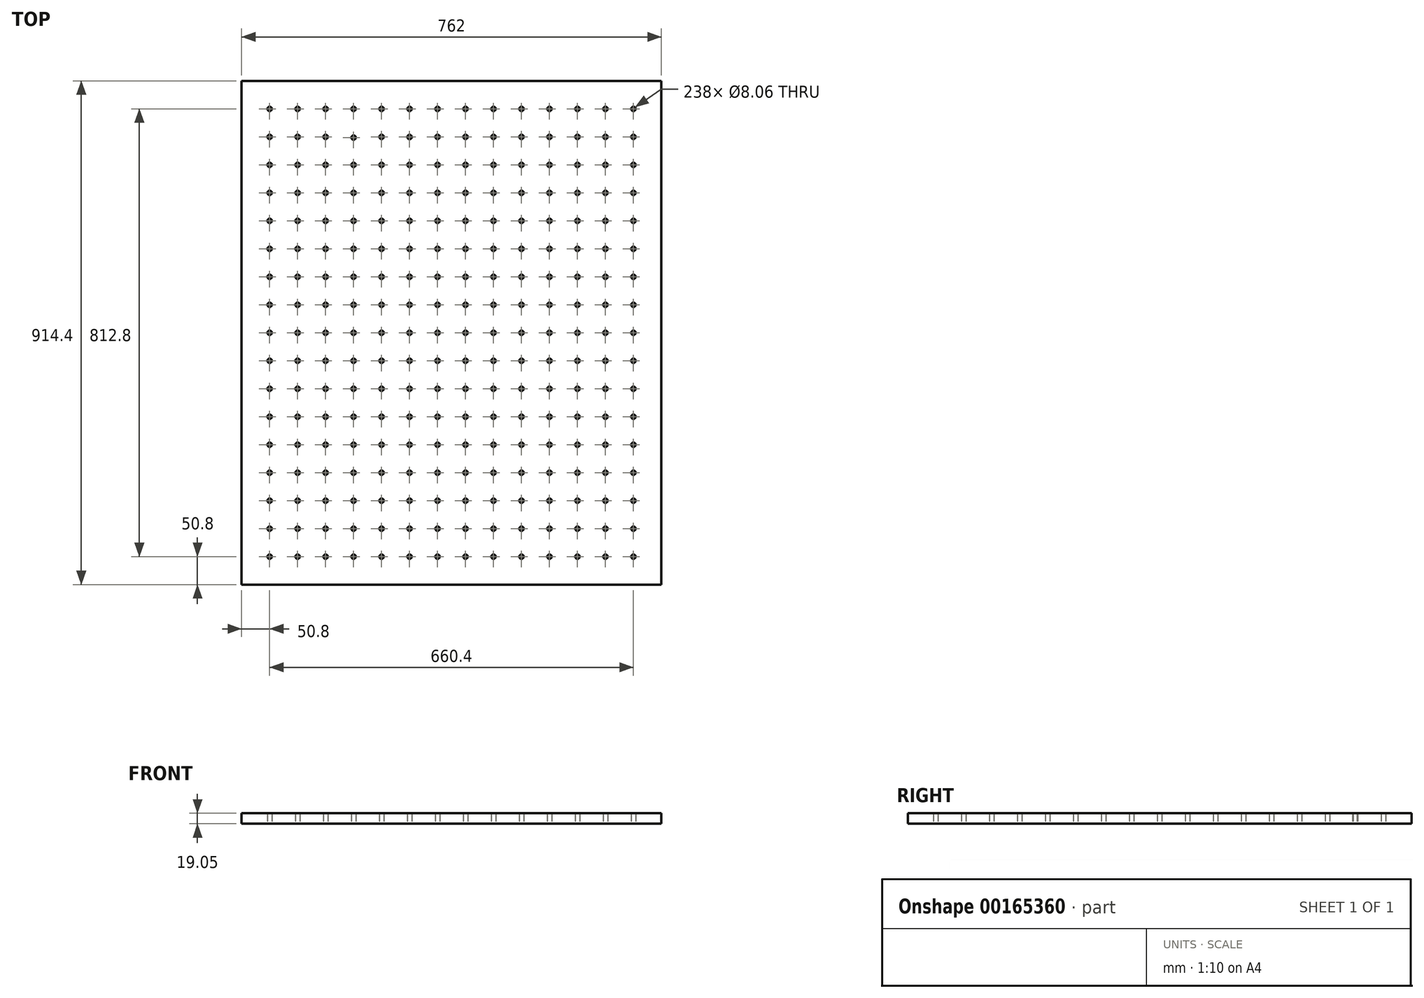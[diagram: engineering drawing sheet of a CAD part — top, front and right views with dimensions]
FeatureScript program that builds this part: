
annotation { "Feature Type Name" : "Feature", "Feature Type Description" : "" }
export const myFeature = defineFeature(function(context is Context, id is Id, definition is map)
    precondition{}
    {
        {
            var Q0;
            Q0=qCreatedBy(makeId("Top.planeOp"),FACE);
            var sketch = newSketch(context, id + "F0", { "sketchPlane" : qUnion([Q0])});
            skLineSegment(sketch, "E0.rect.bottom", {"start": v(381, -457.2) * mm, "end": v(-381, -457.2) * mm});
            skLineSegment(sketch, "E0.rect.top", {"start": v(381, 457.2) * mm, "end": v(-381, 457.2) * mm});
            skLineSegment(sketch, "E0.rect.left", {"start": v(381, -457.2) * mm, "end": v(381, 457.2) * mm});
            skLineSegment(sketch, "E0.rect.right", {"start": v(-381, -457.2) * mm, "end": v(-381, 457.2) * mm});
            skPoint(sketch, "E0.rect.middle", {"position": v(0, 0) * mm});
            skLineSegment(sketch, "E1", {"start": v(-381, 406.4) * mm, "end": v(381, 406.4) * mm, "construction": true});
            skLineSegment(sketch, "E2", {"start": v(381, 406.4) * mm, "end": v(378.47, 409.6) * mm, "construction": true});
            skLineSegment(sketch, "E3", {"start": v(-381, 355.6) * mm, "end": v(381, 355.6) * mm, "construction": true});
            skLineSegment(sketch, "E4", {"start": v(-381, 304.8) * mm, "end": v(381, 304.8) * mm, "construction": true});
            skLineSegment(sketch, "E5", {"start": v(-381, 254) * mm, "end": v(381, 254) * mm, "construction": true});
            skLineSegment(sketch, "E6", {"start": v(-381, 203.2) * mm, "end": v(381, 203.2) * mm, "construction": true});
            skLineSegment(sketch, "E7", {"start": v(-381, 152.4) * mm, "end": v(381, 152.4) * mm, "construction": true});
            skLineSegment(sketch, "E8", {"start": v(-381, 0) * mm, "end": v(381, 0) * mm, "construction": true});
            skLineSegment(sketch, "E9", {"start": v(-381, -50.8) * mm, "end": v(381, -50.8) * mm, "construction": true});
            skLineSegment(sketch, "E10", {"start": v(-381, -101.6) * mm, "end": v(381, -101.6) * mm, "construction": true});
            skLineSegment(sketch, "E11", {"start": v(-381, -152.4) * mm, "end": v(381, -152.4) * mm, "construction": true});
            skLineSegment(sketch, "E12", {"start": v(-330.2, -457.2) * mm, "end": v(-330.2, 457.2) * mm, "construction": true});
            skLineSegment(sketch, "E13", {"start": v(-279.4, 457.2) * mm, "end": v(-279.4, -457.2) * mm, "construction": true});
            skLineSegment(sketch, "E14", {"start": v(-228.6, 457.2) * mm, "end": v(-228.6, -457.2) * mm, "construction": true});
            skLineSegment(sketch, "E15", {"start": v(-177.8, -457.2) * mm, "end": v(-177.8, 457.2) * mm, "construction": true});
            skLineSegment(sketch, "E16", {"start": v(-127, 457.2) * mm, "end": v(-127, -457.2) * mm, "construction": true});
            skLineSegment(sketch, "E17", {"start": v(-76.2, 457.2) * mm, "end": v(-76.2, -457.2) * mm, "construction": true});
            skLineSegment(sketch, "E18", {"start": v(-25.4, 457.2) * mm, "end": v(-25.4, -457.2) * mm, "construction": true});
            skLineSegment(sketch, "E19", {"start": v(25.4, 457.2) * mm, "end": v(25.4, -457.2) * mm, "construction": true});
            skLineSegment(sketch, "E20", {"start": v(76.2, 457.2) * mm, "end": v(76.2, -457.2) * mm, "construction": true});
            skLineSegment(sketch, "E21", {"start": v(127, 457.2) * mm, "end": v(127, -457.2) * mm, "construction": true});
            skLineSegment(sketch, "E22", {"start": v(177.8, 457.2) * mm, "end": v(177.8, -457.2) * mm, "construction": true});
            skLineSegment(sketch, "E23", {"start": v(228.6, 457.2) * mm, "end": v(228.6, -457.2) * mm, "construction": true});
            skLineSegment(sketch, "E24", {"start": v(-381, -203.2) * mm, "end": v(381, -203.2) * mm, "construction": true});
            skLineSegment(sketch, "E25", {"start": v(-381, -254) * mm, "end": v(381, -254) * mm, "construction": true});
            skLineSegment(sketch, "E26", {"start": v(-381, -304.8) * mm, "end": v(381, -304.8) * mm, "construction": true});
            skLineSegment(sketch, "E27", {"start": v(-381, -355.6) * mm, "end": v(381, -355.6) * mm, "construction": true});
            skLineSegment(sketch, "E28", {"start": v(-381, -406.4) * mm, "end": v(381, -406.4) * mm, "construction": true});
            skLineSegment(sketch, "E29", {"start": v(-381, 101.6) * mm, "end": v(381, 101.6) * mm, "construction": true});
            skLineSegment(sketch, "E30", {"start": v(-381, 50.8) * mm, "end": v(381, 50.8) * mm, "construction": true});
            skLineSegment(sketch, "E31", {"start": v(279.4, 457.2) * mm, "end": v(279.4, -457.2) * mm, "construction": true});
            skLineSegment(sketch, "E32", {"start": v(330.2, 457.2) * mm, "end": v(330.2, -457.2) * mm, "construction": true});
            skCircle(sketch, "E33", {"center": v(-330.2, 406.4) * mm, "radius": 4.03 * mm});
            skCircle(sketch, "E34", {"center": v(-279.4, 406.4) * mm, "radius": 4.03 * mm});
            skCircle(sketch, "E35", {"center": v(-228.6, 406.4) * mm, "radius": 4.03 * mm});
            skCircle(sketch, "E36", {"center": v(-177.8, 406.4) * mm, "radius": 4.03 * mm});
            skCircle(sketch, "E37", {"center": v(-127, 406.4) * mm, "radius": 4.03 * mm});
            skCircle(sketch, "E38", {"center": v(-76.2, 406.4) * mm, "radius": 4.03 * mm});
            skCircle(sketch, "E39", {"center": v(-25.4, 406.4) * mm, "radius": 4.03 * mm});
            skCircle(sketch, "E40", {"center": v(25.4, 406.4) * mm, "radius": 4.03 * mm});
            skCircle(sketch, "E41", {"center": v(76.2, 406.4) * mm, "radius": 4.03 * mm});
            skCircle(sketch, "E42", {"center": v(127, 406.4) * mm, "radius": 4.03 * mm});
            skCircle(sketch, "E43", {"center": v(177.8, 406.4) * mm, "radius": 4.03 * mm});
            skCircle(sketch, "E44", {"center": v(-330.2, 355.6) * mm, "radius": 4.03 * mm});
            skCircle(sketch, "E45", {"center": v(-279.4, 355.6) * mm, "radius": 4.03 * mm});
            skCircle(sketch, "E46", {"center": v(-228.6, 355.6) * mm, "radius": 4.03 * mm});
            skCircle(sketch, "E47", {"center": v(-177.8, 354.31) * mm, "radius": 4.03 * mm});
            skCircle(sketch, "E48", {"center": v(-127, 355.6) * mm, "radius": 4.03 * mm});
            skCircle(sketch, "E49", {"center": v(-76.2, 355.32) * mm, "radius": 4.03 * mm});
            skCircle(sketch, "E50", {"center": v(-25.4, 355.6) * mm, "radius": 4.03 * mm});
            skCircle(sketch, "E51", {"center": v(25.4, 355.6) * mm, "radius": 4.03 * mm});
            skCircle(sketch, "E52", {"center": v(76.2, 355.6) * mm, "radius": 4.03 * mm});
            skCircle(sketch, "E53", {"center": v(127, 355.6) * mm, "radius": 4.03 * mm});
            skCircle(sketch, "E54", {"center": v(177.8, 355.6) * mm, "radius": 4.03 * mm});
            skCircle(sketch, "E55", {"center": v(228.6, 355.6) * mm, "radius": 4.03 * mm});
            skCircle(sketch, "E56", {"center": v(228.6, 304.8) * mm, "radius": 4.03 * mm});
            skCircle(sketch, "E57", {"center": v(177.8, 304.8) * mm, "radius": 4.03 * mm});
            skCircle(sketch, "E58", {"center": v(127, 304.8) * mm, "radius": 4.03 * mm});
            skCircle(sketch, "E59", {"center": v(76.2, 304.8) * mm, "radius": 4.03 * mm});
            skCircle(sketch, "E60", {"center": v(-330.2, 304.8) * mm, "radius": 4.03 * mm});
            skCircle(sketch, "E61", {"center": v(-279.4, 304.8) * mm, "radius": 4.03 * mm});
            skCircle(sketch, "E62", {"center": v(-228.6, 304.8) * mm, "radius": 4.03 * mm});
            skCircle(sketch, "E63", {"center": v(-177.8, 304.8) * mm, "radius": 4.03 * mm});
            skCircle(sketch, "E64", {"center": v(-127, 304.8) * mm, "radius": 4.03 * mm});
            skCircle(sketch, "E65", {"center": v(-76.2, 304.8) * mm, "radius": 4.03 * mm});
            skCircle(sketch, "E66", {"center": v(-25.4, 304.8) * mm, "radius": 4.03 * mm});
            skCircle(sketch, "E67", {"center": v(25.4, 304.8) * mm, "radius": 4.03 * mm});
            skCircle(sketch, "E68", {"center": v(-330.2, 254) * mm, "radius": 4.03 * mm});
            skCircle(sketch, "E69", {"center": v(-279.4, 254) * mm, "radius": 4.03 * mm});
            skCircle(sketch, "E70", {"center": v(-228.6, 254) * mm, "radius": 4.03 * mm});
            skCircle(sketch, "E71", {"center": v(-177.8, 254) * mm, "radius": 4.03 * mm});
            skCircle(sketch, "E72", {"center": v(-127, 254) * mm, "radius": 4.03 * mm});
            skCircle(sketch, "E73", {"center": v(-76.2, 254) * mm, "radius": 4.03 * mm});
            skCircle(sketch, "E74", {"center": v(-25.4, 254) * mm, "radius": 4.03 * mm});
            skCircle(sketch, "E75", {"center": v(25.4, 254) * mm, "radius": 4.03 * mm});
            skCircle(sketch, "E76", {"center": v(76.2, 254) * mm, "radius": 4.03 * mm});
            skCircle(sketch, "E77", {"center": v(127, 254) * mm, "radius": 4.03 * mm});
            skCircle(sketch, "E78", {"center": v(177.8, 254) * mm, "radius": 4.03 * mm});
            skCircle(sketch, "E79", {"center": v(228.6, 254) * mm, "radius": 4.03 * mm});
            skCircle(sketch, "E80", {"center": v(228.6, 203.2) * mm, "radius": 4.03 * mm});
            skCircle(sketch, "E81", {"center": v(177.8, 203.2) * mm, "radius": 4.03 * mm});
            skCircle(sketch, "E82", {"center": v(127, 203.2) * mm, "radius": 4.03 * mm});
            skCircle(sketch, "E83", {"center": v(76.2, 203.2) * mm, "radius": 4.03 * mm});
            skCircle(sketch, "E84", {"center": v(25.4, 203.2) * mm, "radius": 4.03 * mm});
            skCircle(sketch, "E85", {"center": v(-25.4, 203.2) * mm, "radius": 4.03 * mm});
            skCircle(sketch, "E86", {"center": v(-76.2, 203.2) * mm, "radius": 4.03 * mm});
            skCircle(sketch, "E87", {"center": v(-127, 203.2) * mm, "radius": 4.03 * mm});
            skCircle(sketch, "E88", {"center": v(-177.8, 203.2) * mm, "radius": 4.03 * mm});
            skCircle(sketch, "E89", {"center": v(-228.6, 203.2) * mm, "radius": 4.03 * mm});
            skCircle(sketch, "E90", {"center": v(-279.4, 203.2) * mm, "radius": 4.03 * mm});
            skCircle(sketch, "E91", {"center": v(-330.2, 203.2) * mm, "radius": 4.03 * mm});
            skCircle(sketch, "E92", {"center": v(-330.2, 152.4) * mm, "radius": 4.03 * mm});
            skCircle(sketch, "E93", {"center": v(-279.4, 152.4) * mm, "radius": 4.03 * mm});
            skCircle(sketch, "E94", {"center": v(-228.6, 152.4) * mm, "radius": 4.03 * mm});
            skCircle(sketch, "E95", {"center": v(-177.8, 152.4) * mm, "radius": 4.03 * mm});
            skCircle(sketch, "E96", {"center": v(-127, 152.4) * mm, "radius": 4.03 * mm});
            skCircle(sketch, "E97", {"center": v(-76.2, 152.4) * mm, "radius": 4.03 * mm});
            skCircle(sketch, "E98", {"center": v(-25.4, 152.4) * mm, "radius": 4.03 * mm});
            skCircle(sketch, "E99", {"center": v(25.4, 152.4) * mm, "radius": 4.03 * mm});
            skCircle(sketch, "E100", {"center": v(76.2, 152.4) * mm, "radius": 4.03 * mm});
            skCircle(sketch, "E101", {"center": v(127, 152.4) * mm, "radius": 4.03 * mm});
            skCircle(sketch, "E102", {"center": v(177.8, 152.4) * mm, "radius": 4.03 * mm});
            skCircle(sketch, "E103", {"center": v(228.6, 152.4) * mm, "radius": 4.03 * mm});
            skCircle(sketch, "E104", {"center": v(228.6, 101.6) * mm, "radius": 4.03 * mm});
            skCircle(sketch, "E105", {"center": v(177.8, 101.6) * mm, "radius": 4.03 * mm});
            skCircle(sketch, "E106", {"center": v(127, 101.6) * mm, "radius": 4.03 * mm});
            skCircle(sketch, "E107", {"center": v(76.2, 101.6) * mm, "radius": 4.03 * mm});
            skCircle(sketch, "E108", {"center": v(25.4, 101.6) * mm, "radius": 4.03 * mm});
            skCircle(sketch, "E109", {"center": v(-330.2, 101.6) * mm, "radius": 4.03 * mm});
            skCircle(sketch, "E110", {"center": v(-279.4, 101.6) * mm, "radius": 4.03 * mm});
            skCircle(sketch, "E111", {"center": v(-228.6, 101.6) * mm, "radius": 4.03 * mm});
            skCircle(sketch, "E112", {"center": v(-177.8, 101.6) * mm, "radius": 4.03 * mm});
            skCircle(sketch, "E113", {"center": v(-127, 101.6) * mm, "radius": 4.03 * mm});
            skCircle(sketch, "E114", {"center": v(-76.2, 101.6) * mm, "radius": 4.03 * mm});
            skCircle(sketch, "E115", {"center": v(-330.2, 50.8) * mm, "radius": 4.03 * mm});
            skCircle(sketch, "E116", {"center": v(-279.4, 50.8) * mm, "radius": 4.03 * mm});
            skCircle(sketch, "E117", {"center": v(-228.6, 50.8) * mm, "radius": 4.03 * mm});
            skCircle(sketch, "E118", {"center": v(-177.8, 50.8) * mm, "radius": 4.03 * mm});
            skCircle(sketch, "E119", {"center": v(-127, 50.8) * mm, "radius": 4.03 * mm});
            skCircle(sketch, "E120", {"center": v(-76.2, 50.8) * mm, "radius": 4.03 * mm});
            skCircle(sketch, "E121", {"center": v(-25.4, 50.8) * mm, "radius": 4.03 * mm});
            skCircle(sketch, "E122", {"center": v(25.4, 50.8) * mm, "radius": 4.03 * mm});
            skCircle(sketch, "E123", {"center": v(76.2, 50.8) * mm, "radius": 4.03 * mm});
            skCircle(sketch, "E124", {"center": v(127, 50.8) * mm, "radius": 4.03 * mm});
            skCircle(sketch, "E125", {"center": v(177.8, 50.8) * mm, "radius": 4.03 * mm});
            skCircle(sketch, "E126", {"center": v(228.6, 50.8) * mm, "radius": 4.03 * mm});
            skCircle(sketch, "E127", {"center": v(228.6, 406.4) * mm, "radius": 4.03 * mm});
            skCircle(sketch, "E128", {"center": v(279.4, 406.4) * mm, "radius": 4.03 * mm});
            skCircle(sketch, "E129", {"center": v(330.2, 406.4) * mm, "radius": 4.03 * mm});
            skCircle(sketch, "E130", {"center": v(330.2, 355.6) * mm, "radius": 4.03 * mm});
            skCircle(sketch, "E131", {"center": v(279.4, 355.6) * mm, "radius": 4.03 * mm});
            skCircle(sketch, "E132", {"center": v(279.4, 304.8) * mm, "radius": 4.03 * mm});
            skCircle(sketch, "E133", {"center": v(330.2, 304.8) * mm, "radius": 4.03 * mm});
            skCircle(sketch, "E134", {"center": v(279.4, 254) * mm, "radius": 4.03 * mm});
            skCircle(sketch, "E135", {"center": v(330.2, 254) * mm, "radius": 4.03 * mm});
            skCircle(sketch, "E136", {"center": v(330.2, 203.2) * mm, "radius": 4.03 * mm});
            skCircle(sketch, "E137", {"center": v(279.4, 203.2) * mm, "radius": 4.03 * mm});
            skCircle(sketch, "E138", {"center": v(279.4, 152.4) * mm, "radius": 4.03 * mm});
            skCircle(sketch, "E139", {"center": v(330.2, 152.4) * mm, "radius": 4.03 * mm});
            skCircle(sketch, "E140", {"center": v(279.4, 101.6) * mm, "radius": 4.03 * mm});
            skCircle(sketch, "E141", {"center": v(330.2, 101.6) * mm, "radius": 4.03 * mm});
            skCircle(sketch, "E142", {"center": v(330.2, 50.8) * mm, "radius": 4.03 * mm});
            skCircle(sketch, "E143", {"center": v(279.4, 50.8) * mm, "radius": 4.03 * mm});
            skCircle(sketch, "E144", {"center": v(330.2, 0) * mm, "radius": 4.03 * mm});
            skCircle(sketch, "E145", {"center": v(279.4, 0) * mm, "radius": 4.03 * mm});
            skCircle(sketch, "E146", {"center": v(228.6, 0) * mm, "radius": 4.03 * mm});
            skCircle(sketch, "E147", {"center": v(177.8, 0) * mm, "radius": 4.03 * mm});
            skCircle(sketch, "E148", {"center": v(127, 0) * mm, "radius": 4.03 * mm});
            skCircle(sketch, "E149", {"center": v(76.2, 0) * mm, "radius": 4.03 * mm});
            skCircle(sketch, "E150", {"center": v(25.4, 0) * mm, "radius": 4.03 * mm});
            skCircle(sketch, "E151", {"center": v(-25.4, 0) * mm, "radius": 4.03 * mm});
            skCircle(sketch, "E152", {"center": v(-76.2, 0) * mm, "radius": 4.03 * mm});
            skCircle(sketch, "E153", {"center": v(-127, 0) * mm, "radius": 4.03 * mm});
            skCircle(sketch, "E154", {"center": v(-177.8, 0) * mm, "radius": 4.03 * mm});
            skCircle(sketch, "E155", {"center": v(-228.6, 0) * mm, "radius": 4.03 * mm});
            skCircle(sketch, "E156", {"center": v(-279.4, 0) * mm, "radius": 4.03 * mm});
            skCircle(sketch, "E157", {"center": v(-330.2, 0) * mm, "radius": 4.03 * mm});
            skCircle(sketch, "E158", {"center": v(-330.2, -50.8) * mm, "radius": 4.03 * mm});
            skCircle(sketch, "E159", {"center": v(-279.4, -50.8) * mm, "radius": 4.03 * mm});
            skCircle(sketch, "E160", {"center": v(-228.6, -50.8) * mm, "radius": 4.03 * mm});
            skCircle(sketch, "E161", {"center": v(-177.8, -50.8) * mm, "radius": 4.03 * mm});
            skCircle(sketch, "E162", {"center": v(-127, -50.8) * mm, "radius": 4.03 * mm});
            skCircle(sketch, "E163", {"center": v(-76.2, -50.8) * mm, "radius": 4.03 * mm});
            skCircle(sketch, "E164", {"center": v(-25.4, -50.8) * mm, "radius": 4.03 * mm});
            skCircle(sketch, "E165", {"center": v(25.4, -50.8) * mm, "radius": 4.03 * mm});
            skCircle(sketch, "E166", {"center": v(76.2, -50.8) * mm, "radius": 4.03 * mm});
            skCircle(sketch, "E167", {"center": v(127, -50.8) * mm, "radius": 4.03 * mm});
            skCircle(sketch, "E168", {"center": v(177.8, -50.8) * mm, "radius": 4.03 * mm});
            skCircle(sketch, "E169", {"center": v(228.6, -50.8) * mm, "radius": 4.03 * mm});
            skCircle(sketch, "E170", {"center": v(279.4, -50.8) * mm, "radius": 4.03 * mm});
            skCircle(sketch, "E171", {"center": v(330.2, -50.8) * mm, "radius": 4.03 * mm});
            skCircle(sketch, "E172", {"center": v(-330.2, -101.6) * mm, "radius": 4.03 * mm});
            skCircle(sketch, "E173", {"center": v(-279.4, -101.6) * mm, "radius": 4.03 * mm});
            skCircle(sketch, "E174", {"center": v(-228.6, -101.6) * mm, "radius": 4.03 * mm});
            skCircle(sketch, "E175", {"center": v(-177.8, -101.6) * mm, "radius": 4.03 * mm});
            skCircle(sketch, "E176", {"center": v(-127, -101.6) * mm, "radius": 4.03 * mm});
            skCircle(sketch, "E177", {"center": v(-76.2, -101.6) * mm, "radius": 4.03 * mm});
            skCircle(sketch, "E178", {"center": v(-25.4, -101.6) * mm, "radius": 4.03 * mm});
            skCircle(sketch, "E179", {"center": v(25.4, -101.6) * mm, "radius": 4.03 * mm});
            skCircle(sketch, "E180", {"center": v(76.2, -101.6) * mm, "radius": 4.03 * mm});
            skCircle(sketch, "E181", {"center": v(127, -101.6) * mm, "radius": 4.03 * mm});
            skCircle(sketch, "E182", {"center": v(177.8, -101.6) * mm, "radius": 4.03 * mm});
            skCircle(sketch, "E183", {"center": v(228.6, -101.6) * mm, "radius": 4.03 * mm});
            skCircle(sketch, "E184", {"center": v(279.4, -101.6) * mm, "radius": 4.03 * mm});
            skCircle(sketch, "E185", {"center": v(330.2, -101.6) * mm, "radius": 4.03 * mm});
            skCircle(sketch, "E186", {"center": v(-330.2, -152.4) * mm, "radius": 4.03 * mm});
            skCircle(sketch, "E187", {"center": v(-279.4, -152.4) * mm, "radius": 4.03 * mm});
            skCircle(sketch, "E188", {"center": v(-228.6, -152.4) * mm, "radius": 4.03 * mm});
            skCircle(sketch, "E189", {"center": v(-177.8, -152.4) * mm, "radius": 4.03 * mm});
            skCircle(sketch, "E190", {"center": v(-127, -152.4) * mm, "radius": 4.03 * mm});
            skCircle(sketch, "E191", {"center": v(-76.2, -152.4) * mm, "radius": 4.03 * mm});
            skCircle(sketch, "E192", {"center": v(-25.4, -152.4) * mm, "radius": 4.03 * mm});
            skCircle(sketch, "E193", {"center": v(25.4, -152.4) * mm, "radius": 4.03 * mm});
            skCircle(sketch, "E194", {"center": v(76.2, -152.4) * mm, "radius": 4.03 * mm});
            skCircle(sketch, "E195", {"center": v(127, -152.4) * mm, "radius": 4.03 * mm});
            skCircle(sketch, "E196", {"center": v(177.8, -152.4) * mm, "radius": 4.03 * mm});
            skCircle(sketch, "E197", {"center": v(228.6, -152.4) * mm, "radius": 4.03 * mm});
            skCircle(sketch, "E198", {"center": v(279.4, -152.4) * mm, "radius": 4.03 * mm});
            skCircle(sketch, "E199", {"center": v(330.2, -152.4) * mm, "radius": 4.03 * mm});
            skCircle(sketch, "E200", {"center": v(-330.2, -203.2) * mm, "radius": 4.03 * mm});
            skCircle(sketch, "E201", {"center": v(-279.4, -203.2) * mm, "radius": 4.03 * mm});
            skCircle(sketch, "E202", {"center": v(-228.6, -203.2) * mm, "radius": 4.03 * mm});
            skCircle(sketch, "E203", {"center": v(-177.8, -203.2) * mm, "radius": 4.03 * mm});
            skCircle(sketch, "E204", {"center": v(-127, -203.2) * mm, "radius": 4.03 * mm});
            skCircle(sketch, "E205", {"center": v(-76.2, -203.2) * mm, "radius": 4.03 * mm});
            skCircle(sketch, "E206", {"center": v(-25.4, -203.2) * mm, "radius": 4.03 * mm});
            skCircle(sketch, "E207", {"center": v(25.4, -203.2) * mm, "radius": 4.03 * mm});
            skCircle(sketch, "E208", {"center": v(76.2, -203.2) * mm, "radius": 4.03 * mm});
            skCircle(sketch, "E209", {"center": v(127, -203.2) * mm, "radius": 4.03 * mm});
            skCircle(sketch, "E210", {"center": v(177.8, -203.2) * mm, "radius": 4.03 * mm});
            skCircle(sketch, "E211", {"center": v(228.6, -203.2) * mm, "radius": 4.03 * mm});
            skCircle(sketch, "E212", {"center": v(279.4, -203.2) * mm, "radius": 4.03 * mm});
            skCircle(sketch, "E213", {"center": v(330.2, -203.2) * mm, "radius": 4.03 * mm});
            skCircle(sketch, "E214", {"center": v(-330.2, -254) * mm, "radius": 4.03 * mm});
            skCircle(sketch, "E215", {"center": v(-279.4, -254) * mm, "radius": 4.03 * mm});
            skCircle(sketch, "E216", {"center": v(-228.6, -254) * mm, "radius": 4.03 * mm});
            skCircle(sketch, "E217", {"center": v(-177.8, -254) * mm, "radius": 4.03 * mm});
            skCircle(sketch, "E218", {"center": v(-127, -254) * mm, "radius": 4.03 * mm});
            skCircle(sketch, "E219", {"center": v(-76.2, -254) * mm, "radius": 4.03 * mm});
            skCircle(sketch, "E220", {"center": v(-25.4, -254) * mm, "radius": 4.03 * mm});
            skCircle(sketch, "E221", {"center": v(25.4, -254) * mm, "radius": 4.03 * mm});
            skCircle(sketch, "E222", {"center": v(76.2, -254) * mm, "radius": 4.03 * mm});
            skCircle(sketch, "E223", {"center": v(127, -254) * mm, "radius": 4.03 * mm});
            skCircle(sketch, "E224", {"center": v(177.8, -254) * mm, "radius": 4.03 * mm});
            skCircle(sketch, "E225", {"center": v(228.6, -254) * mm, "radius": 4.03 * mm});
            skCircle(sketch, "E226", {"center": v(279.4, -254) * mm, "radius": 4.03 * mm});
            skCircle(sketch, "E227", {"center": v(330.2, -254) * mm, "radius": 4.03 * mm});
            skCircle(sketch, "E228", {"center": v(330.2, -304.8) * mm, "radius": 4.03 * mm});
            skCircle(sketch, "E229", {"center": v(-330.2, -304.8) * mm, "radius": 4.03 * mm});
            skCircle(sketch, "E230", {"center": v(-330.2, -355.6) * mm, "radius": 4.03 * mm});
            skCircle(sketch, "E231", {"center": v(-330.2, -406.4) * mm, "radius": 4.03 * mm});
            skCircle(sketch, "E232", {"center": v(-279.4, -304.8) * mm, "radius": 4.03 * mm});
            skCircle(sketch, "E233", {"center": v(-279.4, -355.6) * mm, "radius": 4.03 * mm});
            skCircle(sketch, "E234", {"center": v(-279.4, -406.4) * mm, "radius": 4.03 * mm});
            skCircle(sketch, "E235", {"center": v(-228.6, -304.8) * mm, "radius": 4.03 * mm});
            skCircle(sketch, "E236", {"center": v(-228.6, -355.6) * mm, "radius": 4.03 * mm});
            skCircle(sketch, "E237", {"center": v(-228.6, -406.4) * mm, "radius": 4.03 * mm});
            skCircle(sketch, "E238", {"center": v(-177.8, -304.8) * mm, "radius": 4.03 * mm});
            skCircle(sketch, "E239", {"center": v(-177.8, -355.6) * mm, "radius": 4.03 * mm});
            skCircle(sketch, "E240", {"center": v(-177.8, -406.4) * mm, "radius": 4.03 * mm});
            skCircle(sketch, "E241", {"center": v(-127, -304.8) * mm, "radius": 4.03 * mm});
            skCircle(sketch, "E242", {"center": v(-127, -355.6) * mm, "radius": 4.03 * mm});
            skCircle(sketch, "E243", {"center": v(-127, -406.4) * mm, "radius": 4.03 * mm});
            skCircle(sketch, "E244", {"center": v(-76.2, -304.8) * mm, "radius": 4.03 * mm});
            skCircle(sketch, "E245", {"center": v(-76.2, -355.6) * mm, "radius": 4.03 * mm});
            skCircle(sketch, "E246", {"center": v(-76.2, -406.4) * mm, "radius": 4.03 * mm});
            skCircle(sketch, "E247", {"center": v(-25.4, -304.8) * mm, "radius": 4.03 * mm});
            skCircle(sketch, "E248", {"center": v(-25.4, -355.6) * mm, "radius": 4.03 * mm});
            skCircle(sketch, "E249", {"center": v(-25.4, -406.4) * mm, "radius": 4.03 * mm});
            skCircle(sketch, "E250", {"center": v(25.4, -304.8) * mm, "radius": 4.03 * mm});
            skCircle(sketch, "E251", {"center": v(25.4, -355.6) * mm, "radius": 4.03 * mm});
            skCircle(sketch, "E252", {"center": v(25.4, -406.4) * mm, "radius": 4.03 * mm});
            skCircle(sketch, "E253", {"center": v(76.2, -304.8) * mm, "radius": 4.03 * mm});
            skCircle(sketch, "E254", {"center": v(76.2, -355.6) * mm, "radius": 4.03 * mm});
            skCircle(sketch, "E255", {"center": v(76.2, -406.4) * mm, "radius": 4.03 * mm});
            skCircle(sketch, "E256", {"center": v(127, -304.8) * mm, "radius": 4.03 * mm});
            skCircle(sketch, "E257", {"center": v(127, -355.6) * mm, "radius": 4.03 * mm});
            skCircle(sketch, "E258", {"center": v(127, -406.4) * mm, "radius": 4.03 * mm});
            skCircle(sketch, "E259", {"center": v(177.8, -304.8) * mm, "radius": 4.03 * mm});
            skCircle(sketch, "E260", {"center": v(177.8, -355.6) * mm, "radius": 4.03 * mm});
            skCircle(sketch, "E261", {"center": v(177.8, -406.4) * mm, "radius": 4.03 * mm});
            skCircle(sketch, "E262", {"center": v(228.6, -304.8) * mm, "radius": 4.03 * mm});
            skCircle(sketch, "E263", {"center": v(228.6, -355.6) * mm, "radius": 4.03 * mm});
            skCircle(sketch, "E264", {"center": v(228.6, -406.4) * mm, "radius": 4.03 * mm});
            skCircle(sketch, "E265", {"center": v(279.4, -304.8) * mm, "radius": 4.03 * mm});
            skCircle(sketch, "E266", {"center": v(279.4, -355.6) * mm, "radius": 4.03 * mm});
            skCircle(sketch, "E267", {"center": v(279.4, -406.4) * mm, "radius": 4.03 * mm});
            skCircle(sketch, "E268", {"center": v(330.2, -355.6) * mm, "radius": 4.03 * mm});
            skCircle(sketch, "E269", {"center": v(330.2, -406.4) * mm, "radius": 4.03 * mm});
            skCircle(sketch, "E270", {"center": v(-25.4, 101.6) * mm, "radius": 4.03 * mm});
            skSolve(sketch);
        }
        {
            var Q0;
            Q0=qSketchRegion(id+"F0",true);
            extrude(context, id + "F1", {"entities" : qUnion([Q0]), "depth" : 19.05 * mm});
        }
    });
